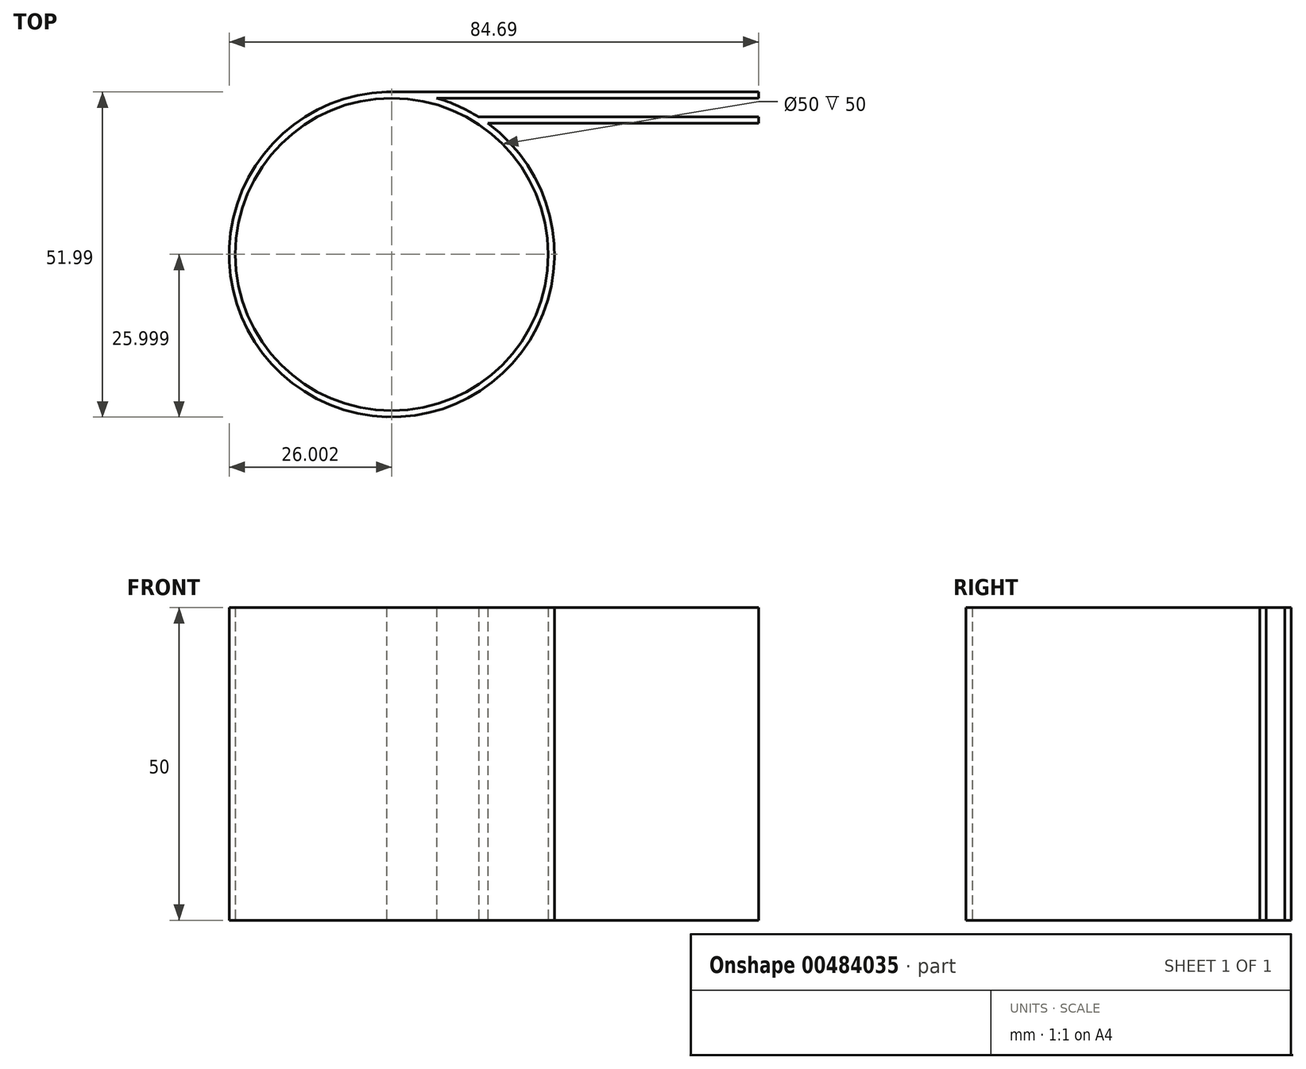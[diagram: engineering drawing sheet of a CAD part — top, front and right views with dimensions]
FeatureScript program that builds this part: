
annotation { "Feature Type Name" : "Feature", "Feature Type Description" : "" }
export const myFeature = defineFeature(function(context is Context, id is Id, definition is map)
    precondition{}
    {
        {
            var Q0;
            Q0=qCreatedBy(makeId("Top.planeOp"),FACE);
            var sketch = newSketch(context, id + "F0", { "sketchPlane" : qUnion([Q0])});
            skCircle(sketch, "E0", {"center": v(-9.36, 14.47) * mm, "radius": 25 * mm});
            skArc(sketch, "E1.0", {"start": v(-10.17, 40.46) * mm, "mid": v(-17.04, -10.37) * mm, "end": v(5.99, 35.46) * mm});
            skLineSegment(sketch, "E2.top", {"start": v(-10.17, 40.46) * mm, "end": v(49.33, 40.46) * mm});
            skLineSegment(sketch, "E2.left", {"start": v(-10.16, 40.96) * mm, "end": v(-10.16, 40.96) * mm});
            skLineSegment(sketch, "E2.right", {"start": v(49.33, 39.46) * mm, "end": v(49.33, 40.46) * mm});
            skPoint(sketch, "E3.visualSharp", {"position": v(-10.16, 40.46) * mm});
            skArc(sketch, "E3.filletArc", {"start": v(-10.18, 39.46) * mm, "mid": v(-10.17, 39.46) * mm, "end": v(-10.16, 39.46) * mm});
            skPoint(sketch, "E4.visualSharp", {"position": v(-10.67, 40.46) * mm});
            skLineSegment(sketch, "E5.1.0.0", {"start": v(4.52, 36.46) * mm, "end": v(49.3, 36.46) * mm});
            skLineSegment(sketch, "E5.1.0.1", {"start": v(5.99, 35.46) * mm, "end": v(49.3, 35.46) * mm});
            skLineSegment(sketch, "E5.1.0.4", {"start": v(49.3, 35.46) * mm, "end": v(49.3, 36.46) * mm});
            skPoint(sketch, "E6.orphan", {"position": v(-10.2, 36.46) * mm});
            skLineSegment(sketch, "E7.trimOffspring", {"start": v(-2.17, 39.46) * mm, "end": v(49.33, 39.46) * mm});
            skPoint(sketch, "E8.orphan", {"position": v(-10.66, 39.96) * mm});
            skArc(sketch, "E9.trimOffspring", {"start": v(4.52, 36.46) * mm, "mid": v(1.28, 38.2) * mm, "end": v(-2.17, 39.46) * mm});
            skSolve(sketch);
        }
        {
            var Q0;
            Q0=makeQuery(id+"F0.imprint","IMPRINT",FACE,{"disambiguationData":[TD([[makeQuery(id+"F0.imprint","IMPRINT",EDGE,{"derivedFrom":sQuery(id+"F0.wireOp",EDGE,"E0")}),1.0]])]});
            var Q1;
            Q1=makeQuery(id+"F0.imprint","IMPRINT",FACE,{"disambiguationData":[TD([[makeQuery(id+"F0.imprint","IMPRINT",EDGE,{"derivedFrom":sQuery(id+"F0.wireOp",EDGE,"E0")}),-1.0]])]});
            extrude(context, id + "F1", {"entities" : qUnion([Q0, Q1]), "depth" : 50 * mm});
        }
        {
            var Q0;
            Q0=sQuery(id+"F0.wireOp",EDGE,"E0");
            extrude(context, id + "F2", {"bodyType" : ToolBodyType.SURFACE, "surfaceEntities" : qUnion([Q0]), "depth" : 50 * mm});
        }
        {
            var Q0;
            Q0=sQuery(id+"F0.wireOp",VERTEX,"E0.center");
            var Q1;
            Q1=makeQuery(id+"F1.opExtrude","SWEPT_BODY",BODY,{"disambiguationData":[OSD([sQuery(id+"F0.wireOp",EDGE,"E1.0"),sQuery(id+"F0.wireOp",EDGE,"E2.top"),sQuery(id+"F0.wireOp",EDGE,"E2.right"),sQuery(id+"F0.wireOp",EDGE,"E5.1.0.0"),sQuery(id+"F0.wireOp",EDGE,"E5.1.0.1"),sQuery(id+"F0.wireOp",EDGE,"E5.1.0.4"),sQuery(id+"F0.wireOp",EDGE,"E7.trimOffspring"),sQuery(id+"F0.wireOp",EDGE,"E9.trimOffspring")])]});
            hole(context, id + "F3", {"style" : HoleStyle.SIMPLE, "endStyle" : HoleEndStyle.THROUGH, "oppositeDirection" : true, "holeDiameter" : 50 * mm, "isTappedThrough" : true, "tappedDepth" : 12 * mm, "tapClearance" : 3, "locations" : qUnion([Q0]), "scope" : qUnion([Q1])});
        }
    });
